# Revit family: 230268MXG04-013_MDTS4224PZ
name_source: partatom
category: Specialty Equipment
units: mm (PartAtom-declared; Revit-internal decimal feet)

## family parameters
Always vertical = Yes
Cut with Voids When Loaded = No
Enable Cutting in Views = No
Maintain Annotation Orientation = No
Part Type = Normal
Room Calculation Point = No
Round Connector Dimension = Use Diameter
Shared = No
Work Plane-Based = No

## types (1)
- MDTS4224PZ
    Accent Material = ARCAT - Metal - Steel - Accent
    Apparent Load = 0 VA
    Back Panel Material = ARCAT - Metal - Steel - Black - Light
    Body Material = ARCAT - Metal - Steel - Grey
    Clearance Material = ARCAT - Clearance
    Default Elevation = 0"
    Depth = 27 1/4"
    Dimension Guide = https://www.whirlpool.com
    Display Unit = ARCAT - Metal - Steel - Black Stainless
    Door Material = ARCAT - Metal - Steel - Gray - Light
    Energy Guide = https://www.whirlpool.com
    Family Name = Built-In Dishwasher
    Feature 1 = Heated Dry with fan
    Feature 2 = Enhanced Wash
    Feature 3 = 10-year limited parts warranty*
    Height = 34 1/2"
    Skid Plate Material = ARCAT - Metal - Steel - Black
    Style Master = ARCAT - Metal - Steel - Black Stainless
    Voltage = 0 V
    Width = 23 7/8"

## geometry (parser evidence)
native form markers: Sweep x11
no freeform markers — native parametric forms only
